# Revit family: Shower-Shower_Trim-KOHLER-Refinia-K-T5319_1
name_source: partatom
category: Plumbing Fixtures
revit_build: Autodesk Revit 2015 (Build: 20140606_1530(x64)
units: mm (PartAtom-declared; Revit-internal decimal feet)

## types (4) — shared parameters
ADA Compliant = No
Assembly Code = D2010700
CW Connection = No
Cold Water Inlet = Cold Water Inlet
Date Modified = 06/27/2019
Default Elevation = 42"
Description = Shower trim set with push-button diverter, valve not included
Drain Included = No
HW Connection = Yes
Handle Clearance = 3 5/16"
Height = 6 7/16"
Hot Water Inlet = Hot Water Inlet
Manufacturer = KOHLER Co.
MasterFormat 1995 = 15410
MasterFormat 2004 = 22.41.23
Material = Premium Metal Construction
Product Documentation Link = https://www.us.kohler.com
Product Name = Refinia
Product Page URL = http://www.us.kohler.com
Tempered Water Inlet 1 = Tempered Water Inlet 1
URL = https://www.us.kohler.com
Vent Connection = No
Waste Connection = No
Waste Water Outlet = Waste Water Outlet
WaterSense Certified = No
Width = 6 7/16"

## per-type parameters (varying)
| type | Finish | Flow Rate | Height 1 | Length | Model | T5319_4 | T5319_4L | Type |
| With Showerhead,CP-Polished Chrome | Kohler-Metal-CP-Polished_Chrome | 3 GPM | 4 1/8" | 6 3/4" | K-T5319-4-CP | Yes | No | 1 |
| With Showerhead,BN-Vibrant Brushed Nickel | Kohler-Metal-BN-Vibrant_Brushed_Nickel | 3 GPM | 4 1/8" | 6 3/4" | K-T5319-4-BN | Yes | No | 2 |
| Without Showerhead,CP-Polished Chrome | Kohler-Metal-CP-Polished_Chrome | 0 GPM | 1 11/16" | 4 1/2" | K-T5319-4L-CP | No | Yes | 3 |
| Without Showerhead,BN-Vibrant Brushed Nickel | Kohler-Metal-BN-Vibrant_Brushed_Nickel | 0 GPM | 1 11/16" | 4 1/2" | K-T5319-4L-BN | No | Yes | 4 |

## geometry (parser evidence)
native form markers: Sweep x7
no freeform markers — native parametric forms only
